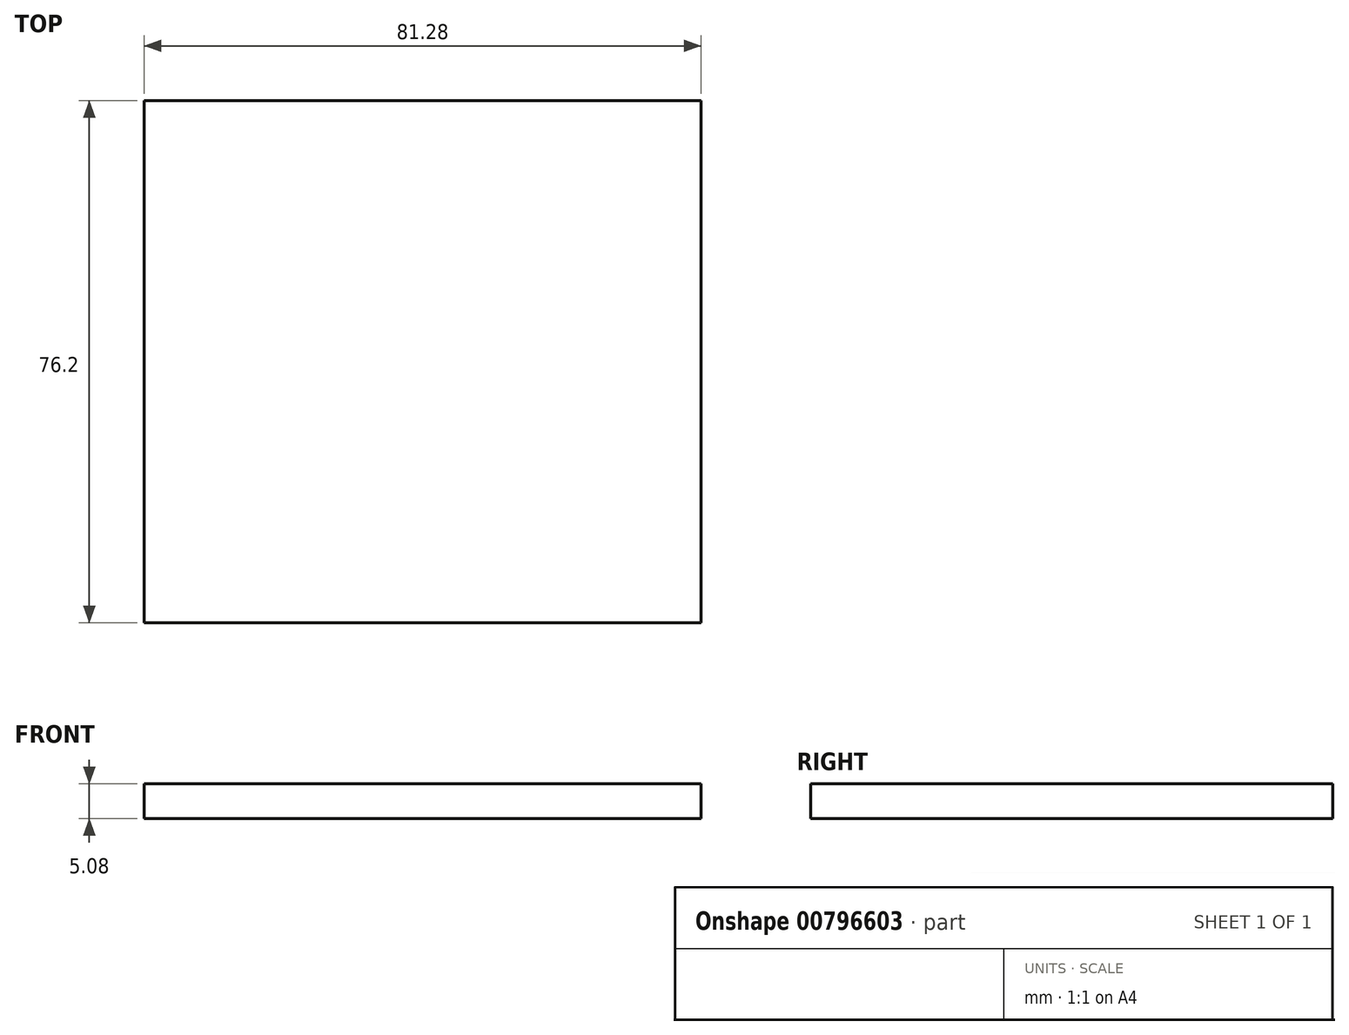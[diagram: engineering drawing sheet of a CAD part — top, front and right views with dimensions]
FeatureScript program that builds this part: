
annotation { "Feature Type Name" : "Feature", "Feature Type Description" : "" }
export const myFeature = defineFeature(function(context is Context, id is Id, definition is map)
    precondition{}
    {
        {
            var Q0;
            Q0=qCreatedBy(makeId("Top.planeOp"),FACE);
            var sketch = newSketch(context, id + "F0", { "sketchPlane" : qUnion([Q0])});
            skLineSegment(sketch, "E0.bottom", {"start": v(40.64, 38.1) * mm, "end": v(-40.64, 38.1) * mm});
            skLineSegment(sketch, "E0.top", {"start": v(40.64, -38.1) * mm, "end": v(-40.64, -38.1) * mm});
            skLineSegment(sketch, "E0.left", {"start": v(40.64, 38.1) * mm, "end": v(40.64, -38.1) * mm});
            skLineSegment(sketch, "E0.right", {"start": v(-40.64, 38.1) * mm, "end": v(-40.64, -38.1) * mm});
            skPoint(sketch, "E0.middle", {"position": v(0, 0) * mm});
            skSolve(sketch);
        }
        {
            var Q0;
            Q0=makeQuery(id+"F0.imprint","IMPRINT",FACE,{"disambiguationData":[TD([[makeQuery(id+"F0.imprint","IMPRINT",EDGE,{"derivedFrom":sQuery(id+"F0.wireOp",EDGE,"E0.bottom")}),1.0]])]});
            extrude(context, id + "F1", {"entities" : qUnion([Q0]), "endBound" : BoundingType.SYMMETRIC, "depth" : 5.08 * mm, "offsetDistance" : 25.4 * mm});
        }
    });
